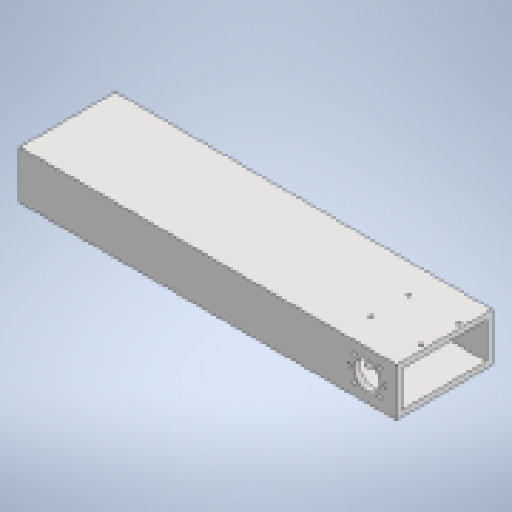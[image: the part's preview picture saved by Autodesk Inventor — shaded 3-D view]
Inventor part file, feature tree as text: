
AUTODESK INVENTOR PART (.ipt)
format: ipt  version: 2023 (Build 270158000, 158)  size: 179,200 bytes
history: native  units: in
note: dims shown in document units (in); Inventor stores cm internally (conversion verified against a paired STEP export)
features: extrude x5, sketch x5, shell x1
ambient origin geometry x8: Origin, YZ Plane, XZ Plane, XY Plane, X Axis, Y Axis, Z Axis, Center Point
bodies: Solid1 (feature_tree)
feature tree (11):
  extrude  "Extrusion1"  Depth=2.0in
  shell  "Shell1"  Thickness=15.748in
  extrude  "Extrusion2"  Depth=0.25in
  extrude  "Extrusion3"  Depth=1.5748in
  extrude  "Extrusion4"  Depth=11.811in TaperAngle=0.0deg
  extrude  "Extrusion5"  Depth=0.3937in
  sketch  "Sketch1"  dims[d0=4.0in d1=2.0in d2=15.748in d3=0.0in]
  sketch  "Sketch2"  dims[d4=0.25in d5=0.1575in]
  sketch  "Sketch3"  dims[d6=2.4803in d7=1.5748in]
  sketch  "Sketch4"  dims[d8=2.0866in d9=11.811in d10=0.0in]
  sketch  "Sketch5"  dims[d11=1.4961in d12=0.1575in d13=45.0deg d14=1.1024in d15=0.3937in d16=0.0in d17=0.6496in d18=0.3937in d19=0.0in d20=0.3937in d22=0.3937in d23=0.0in]
